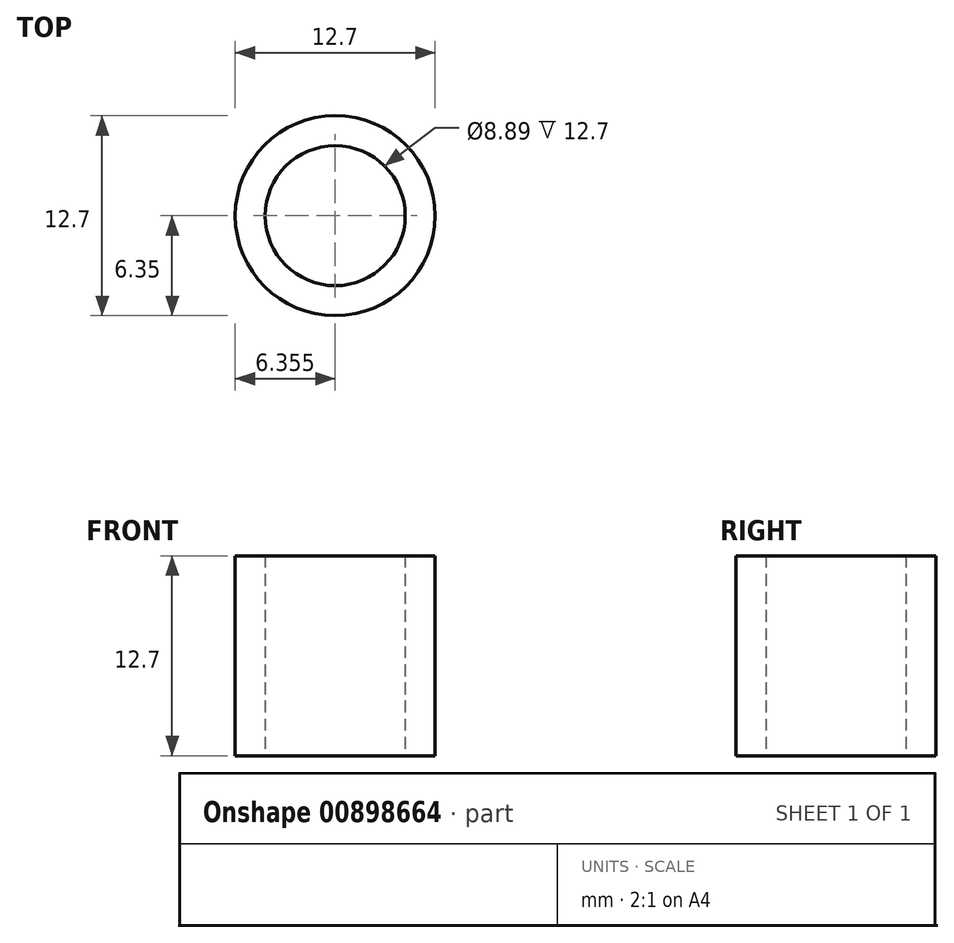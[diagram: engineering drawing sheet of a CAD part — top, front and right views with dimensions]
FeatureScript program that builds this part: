
annotation { "Feature Type Name" : "Feature", "Feature Type Description" : "" }
export const myFeature = defineFeature(function(context is Context, id is Id, definition is map)
    precondition{}
    {
        {
            var Q0;
            Q0=qCreatedBy(makeId("Top.planeOp"),FACE);
            var sketch = newSketch(context, id + "F0", { "sketchPlane" : qUnion([Q0])});
            skCircle(sketch, "E0", {"center": v(-3.7, -0.37) * mm, "radius": 6.35 * mm});
            skCircle(sketch, "E1", {"center": v(-3.7, -0.37) * mm, "radius": 4.45 * mm});
            skSolve(sketch);
        }
        {
            var Q0;
            Q0=makeQuery(id+"F0.imprint","IMPRINT",FACE,{"disambiguationData":[TD([[makeQuery(id+"F0.imprint","IMPRINT",EDGE,{"derivedFrom":sQuery(id+"F0.wireOp",EDGE,"E0")}),-1.0]])]});
            var Q1;
            Q1=makeQuery(id+"F0.imprint","IMPRINT",FACE,{"disambiguationData":[TD([[makeQuery(id+"F0.imprint","IMPRINT",EDGE,{"derivedFrom":sQuery(id+"F0.wireOp",EDGE,"E1")}),-1.0]])]});
            extrude(context, id + "F1", {"entities" : qUnion([Q0, Q1]), "depth" : 12.7 * mm, "offsetDistance" : 25.4 * mm});
        }
    });
